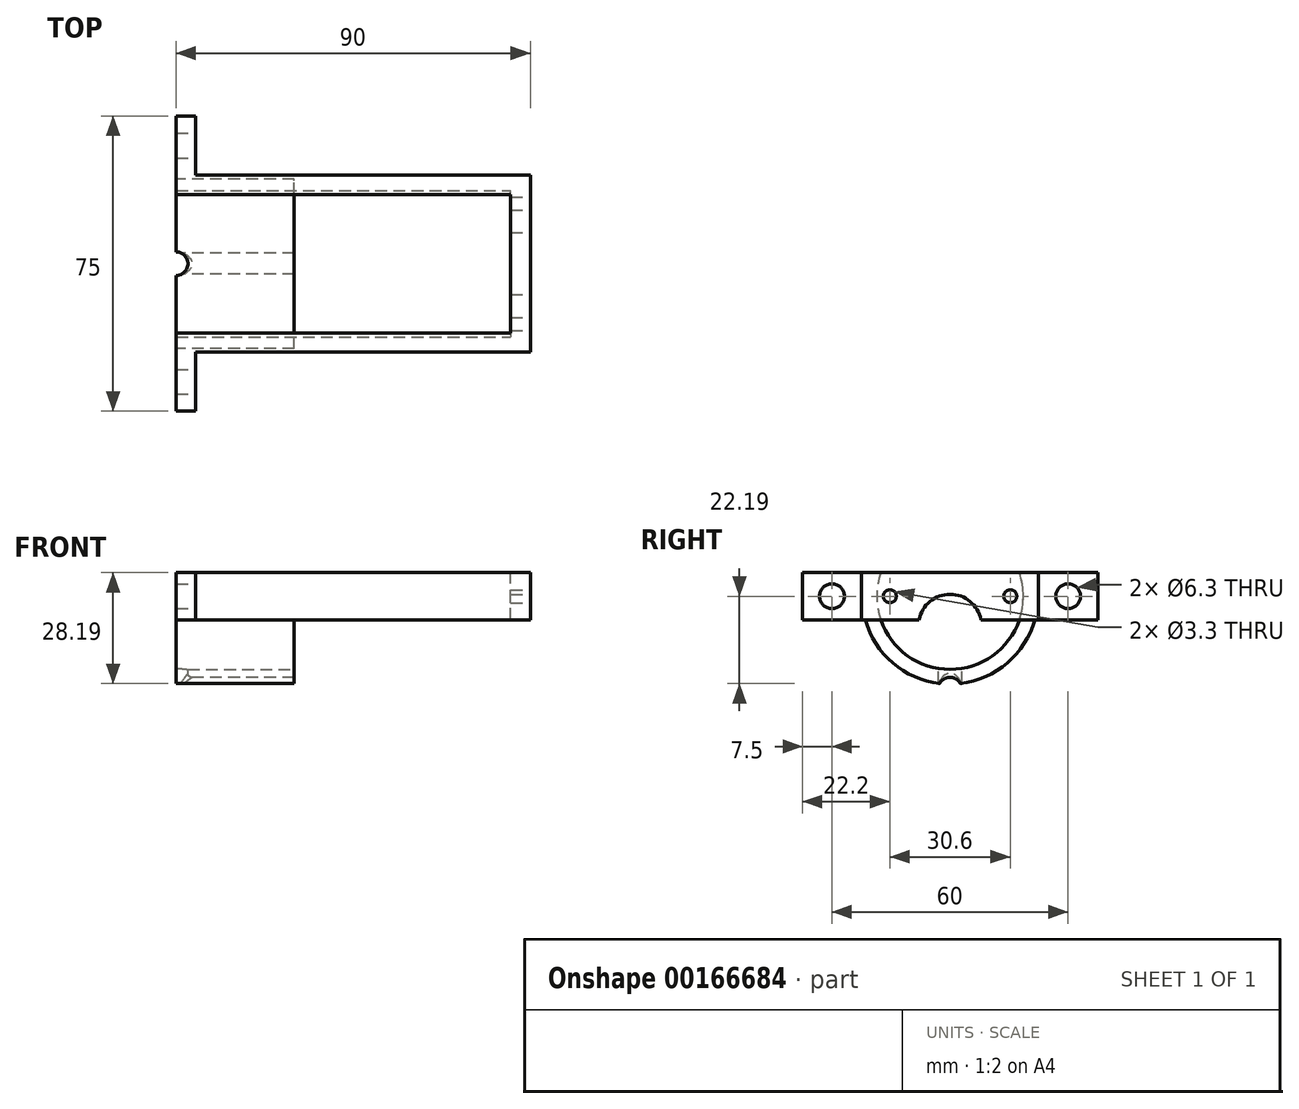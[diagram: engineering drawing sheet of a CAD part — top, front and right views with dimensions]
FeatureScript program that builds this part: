
annotation { "Feature Type Name" : "Feature", "Feature Type Description" : "" }
export const myFeature = defineFeature(function(context is Context, id is Id, definition is map)
    precondition{}
    {
        {
            var Q0;
            Q0=qCreatedBy(makeId("Top.planeOp"),FACE);
            var sketch = newSketch(context, id + "F0", { "sketchPlane" : qUnion([Q0])});
            skLineSegment(sketch, "E0", {"start": v(90, 0) * mm, "end": v(90, -22.5) * mm});
            skLineSegment(sketch, "E1", {"start": v(90, -22.5) * mm, "end": v(5, -22.5) * mm});
            skLineSegment(sketch, "E2", {"start": v(5, -22.5) * mm, "end": v(5, -37.5) * mm});
            skLineSegment(sketch, "E3", {"start": v(5, -37.5) * mm, "end": v(0, -37.5) * mm});
            skLineSegment(sketch, "E4", {"start": v(0, -37.5) * mm, "end": v(0, -17.5) * mm});
            skLineSegment(sketch, "E5", {"start": v(0, -17.5) * mm, "end": v(85, -17.5) * mm});
            skLineSegment(sketch, "E6", {"start": v(85, -17.5) * mm, "end": v(85, 0) * mm});
            skLineSegment(sketch, "E7.MirrorCS", {"start": v(5, 37.5) * mm, "end": v(0, 37.5) * mm});
            skLineSegment(sketch, "E8.MirrorCS", {"start": v(85, 17.5) * mm, "end": v(85, 0) * mm});
            skLineSegment(sketch, "E9.MirrorCS", {"start": v(0, 17.5) * mm, "end": v(85, 17.5) * mm});
            skLineSegment(sketch, "E10.MirrorCS", {"start": v(0, 37.5) * mm, "end": v(0, 17.5) * mm});
            skLineSegment(sketch, "E11.MirrorCS", {"start": v(5, 22.5) * mm, "end": v(5, 37.5) * mm});
            skLineSegment(sketch, "E12.MirrorCS", {"start": v(90, 0) * mm, "end": v(90, 22.5) * mm});
            skLineSegment(sketch, "E13.MirrorCS", {"start": v(90, 22.5) * mm, "end": v(5, 22.5) * mm});
            skLineSegment(sketch, "E14", {"start": v(-47.63, -18.6) * mm, "end": v(121.52, -18.6) * mm, "construction": true});
            skSolve(sketch);
        }
        {
            var Q0;
            Q0=qSketchRegion(id+"F0",true);
            extrude(context, id + "F1", {"entities" : qUnion([Q0]), "depth" : 12 * mm, "symmetric" : true});
        }
        {
            var Q0;
            Q0=makeQuery(id+"F1.opExtrude","SWEPT_FACE",FACE,{"disambiguationData":[OSD([sQuery(id+"F0.wireOp",EDGE,"E0"),sQuery(id+"F0.wireOp",EDGE,"E12.MirrorCS")])]});
            var sketch = newSketch(context, id + "F2", { "sketchPlane" : qUnion([Q0])});
            skCircle(sketch, "E15", {"center": v(-15.3, 0) * mm, "radius": 1.65 * mm});
            skCircle(sketch, "E16", {"center": v(15.3, 0) * mm, "radius": 1.65 * mm});
            skCircle(sketch, "E17", {"center": v(0, -7.5) * mm, "radius": 8 * mm});
            skCircle(sketch, "E18", {"center": v(-30, 0) * mm, "radius": 3.15 * mm});
            skCircle(sketch, "E19", {"center": v(30, 0) * mm, "radius": 3.15 * mm});
            skSolve(sketch);
        }
        {
            var Q0;
            Q0=qSketchRegion(id+"F2",true);
            extrude(context, id + "F3", {"entities" : qUnion([Q0]), "operationType" : NewBodyOperationType.REMOVE, "endBound" : BoundingType.THROUGH_ALL, "oppositeDirection" : true, "depth" : 25 * mm});
        }
        {
            var Q0;
            Q0=makeQuery(id+"F1.opExtrude","SWEPT_FACE",FACE,{"disambiguationData":[OSD([sQuery(id+"F0.wireOp",EDGE,"E6"),sQuery(id+"F0.wireOp",EDGE,"E8.MirrorCS")])]});
            var sketch = newSketch(context, id + "F4", { "sketchPlane" : qUnion([Q0])});
            skCircle(sketch, "E20", {"center": v(0, 0) * mm, "radius": 18.6 * mm});
            skSolve(sketch);
        }
        {
            var Q0;
            Q0=qSketchRegion(id+"F4",true);
            extrude(context, id + "F5", {"entities" : qUnion([Q0]), "operationType" : NewBodyOperationType.REMOVE, "endBound" : BoundingType.THROUGH_ALL, "depth" : 25 * mm});
        }
        {
            var Q0;
            Q0=qCreatedBy(makeId("Right.planeOp"),FACE);
            var sketch = newSketch(context, id + "F6", { "sketchPlane" : qUnion([Q0])});
            skArc(sketch, "E21", {"start": v(-18.6, 0) * mm, "mid": v(0, -18.6) * mm, "end": v(18.6, 0) * mm});
            skArc(sketch, "E22", {"start": v(-22.35, 0) * mm, "mid": v(0, -22.35) * mm, "end": v(22.35, 0) * mm});
            skLineSegment(sketch, "E23", {"start": v(-22.35, 0) * mm, "end": v(-18.6, 0) * mm});
            skLineSegment(sketch, "E24", {"start": v(18.6, 0) * mm, "end": v(22.35, 0) * mm});
            skSolve(sketch);
        }
        {
            var Q0;
            Q0=qSketchRegion(id+"F6",true);
            extrude(context, id + "F7", {"entities" : qUnion([Q0]), "operationType" : NewBodyOperationType.ADD, "depth" : 30 * mm});
        }
        {
            var Q0;
            Q0=qCreatedBy(makeId("Right.planeOp"),FACE);
            var sketch = newSketch(context, id + "F8", { "sketchPlane" : qUnion([Q0])});
            skCircle(sketch, "E25", {"center": v(0, -23.6) * mm, "radius": 3 * mm});
            skSolve(sketch);
        }
        {
            var Q0;
            Q0=qSketchRegion(id+"F8",true);
            extrude(context, id + "F9", {"entities" : qUnion([Q0]), "operationType" : NewBodyOperationType.REMOVE, "endBound" : BoundingType.THROUGH_ALL, "depth" : 25 * mm});
        }
        {
            var Q0;
            Q0=qCreatedBy(makeId("Top.planeOp"),FACE);
            var sketch = newSketch(context, id + "F10", { "sketchPlane" : qUnion([Q0])});
            skCircle(sketch, "E26", {"center": v(0, 0) * mm, "radius": 3 * mm});
            skSolve(sketch);
        }
        {
            var Q0;
            Q0=qSketchRegion(id+"F10",true);
            extrude(context, id + "F11", {"entities" : qUnion([Q0]), "operationType" : NewBodyOperationType.REMOVE, "endBound" : BoundingType.THROUGH_ALL, "oppositeDirection" : true, "depth" : 25 * mm});
        }
        {
            var Q0;
            Q0=makeQuery(id+"F11.boolean.opBoolean","INTERSECT",EDGE,{"derivedFrom":[makeQuery(id+"F9.boolean.opBoolean","COPY",FACE,{"derivedFrom":makeQuery(id+"F9.opExtrude","SWEPT_FACE",FACE,{"disambiguationData":[OSD([sQuery(id+"F8.wireOp",EDGE,"E25")])]})}),makeQuery(id+"F11.opExtrude","SWEPT_FACE",FACE,{"disambiguationData":[OSD([sQuery(id+"F10.wireOp",EDGE,"E26")])]})]});
            fillet(context, id + "F12", {"entities" : qUnion([Q0]), "radius" : 1 * mm, "tangentPropagation" : true, "allowEdgeOverflow" : false});
        }
    });
